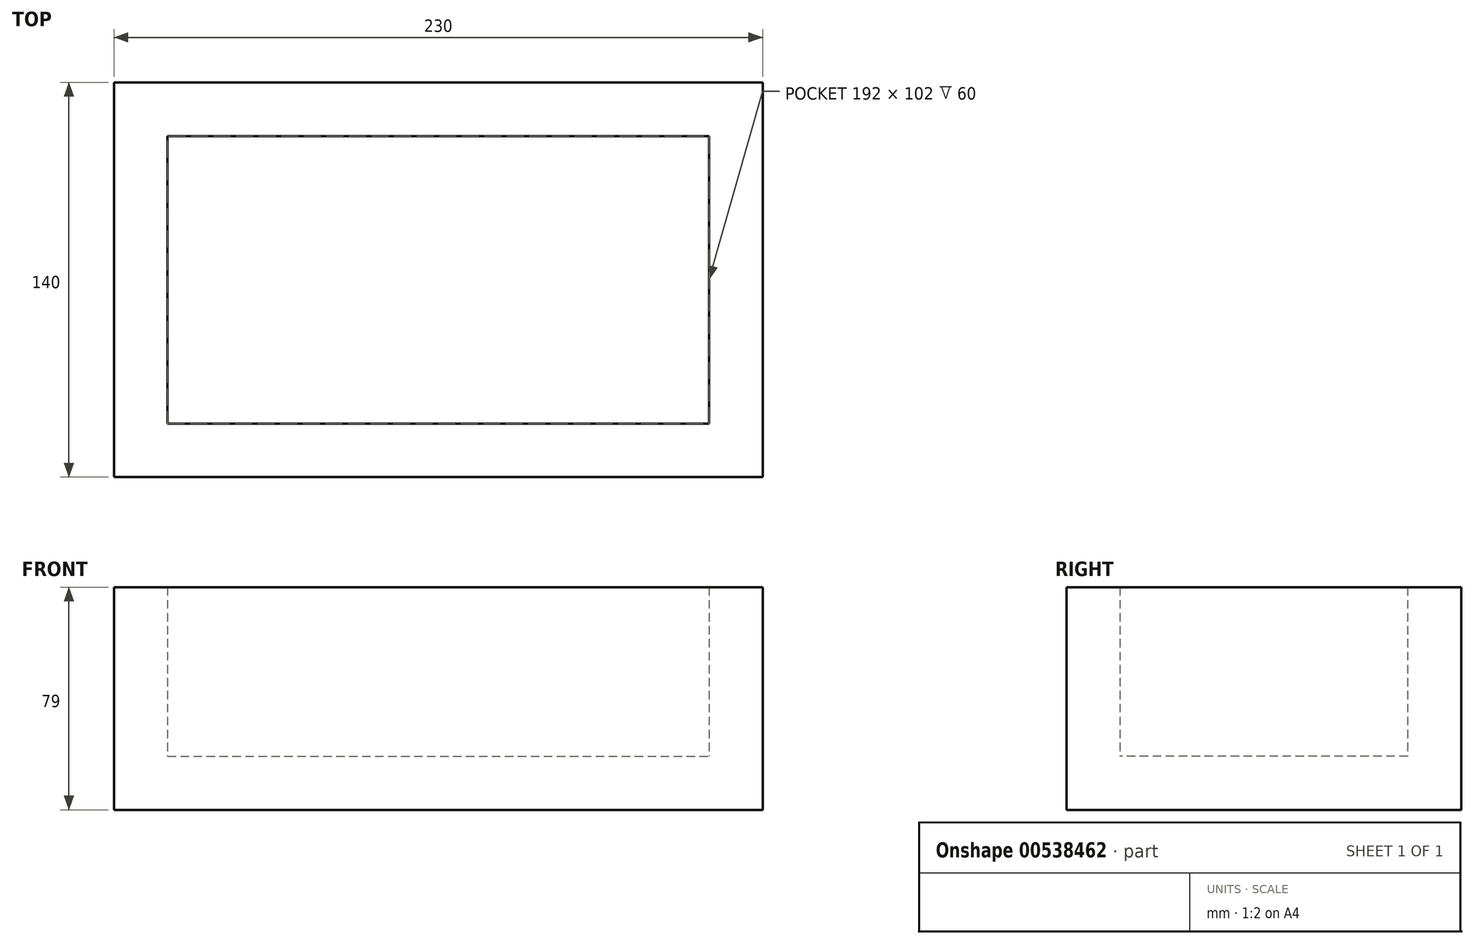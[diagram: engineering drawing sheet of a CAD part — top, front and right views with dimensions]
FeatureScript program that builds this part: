
annotation { "Feature Type Name" : "Feature", "Feature Type Description" : "" }
export const myFeature = defineFeature(function(context is Context, id is Id, definition is map)
    precondition{}
    {
        {
            var Q0;
            Q0=qCreatedBy(makeId("Top.planeOp"),FACE);
            var sketch = newSketch(context, id + "F0", { "sketchPlane" : qUnion([Q0])});
            skLineSegment(sketch, "E0.bottom", {"start": v(115, -70) * mm, "end": v(-115, -70) * mm});
            skLineSegment(sketch, "E0.top", {"start": v(115, 70) * mm, "end": v(-115, 70) * mm});
            skLineSegment(sketch, "E0.left", {"start": v(115, -70) * mm, "end": v(115, 70) * mm});
            skLineSegment(sketch, "E0.right", {"start": v(-115, -70) * mm, "end": v(-115, 70) * mm});
            skPoint(sketch, "E0.middle", {"position": v(0, 0) * mm});
            skSolve(sketch);
        }
        {
            var Q0;
            Q0 = qSketchRegion(id + "F0", true);
            extrude(context, id + "F1", {"entities" : qUnion([Q0]), "depth" : 19 * mm, "offsetDistance" : 25 * mm});
        }
        {
            var Q0;
            Q0=makeQuery(id+"F1.opExtrude","CAP_FACE",FACE,{"disambiguationData":[OSD([sQuery(id+"F0.wireOp",EDGE,"E0.bottom"),sQuery(id+"F0.wireOp",EDGE,"E0.top"),sQuery(id+"F0.wireOp",EDGE,"E0.left"),sQuery(id+"F0.wireOp",EDGE,"E0.right")])],"isStart":false});
            var sketch = newSketch(context, id + "F2", { "sketchPlane" : qUnion([Q0])});
            skLineSegment(sketch, "E1.bottom", {"start": v(-115, -70) * mm, "end": v(115, -70) * mm});
            skLineSegment(sketch, "E1.top", {"start": v(-115, 70) * mm, "end": v(115, 70) * mm});
            skLineSegment(sketch, "E1.left", {"start": v(-115, -70) * mm, "end": v(-115, 70) * mm});
            skLineSegment(sketch, "E1.right", {"start": v(115, -70) * mm, "end": v(115, 70) * mm});
            skLineSegment(sketch, "E2.bottom", {"start": v(-96, 51) * mm, "end": v(96, 51) * mm});
            skLineSegment(sketch, "E2.top", {"start": v(-96, -51) * mm, "end": v(96, -51) * mm});
            skLineSegment(sketch, "E2.left", {"start": v(-96, 51) * mm, "end": v(-96, -51) * mm});
            skLineSegment(sketch, "E2.right", {"start": v(96, 51) * mm, "end": v(96, -51) * mm});
            skPoint(sketch, "E2.middle", {"position": v(0, 0) * mm});
            skSolve(sketch);
        }
        {
            var Q0;
            Q0 = qSketchRegion(id + "F2", true);
            extrude(context, id + "F3", {"entities" : qUnion([Q0]), "operationType" : NewBodyOperationType.ADD, "depth" : 60 * mm, "offsetDistance" : 25 * mm});
        }
    });
